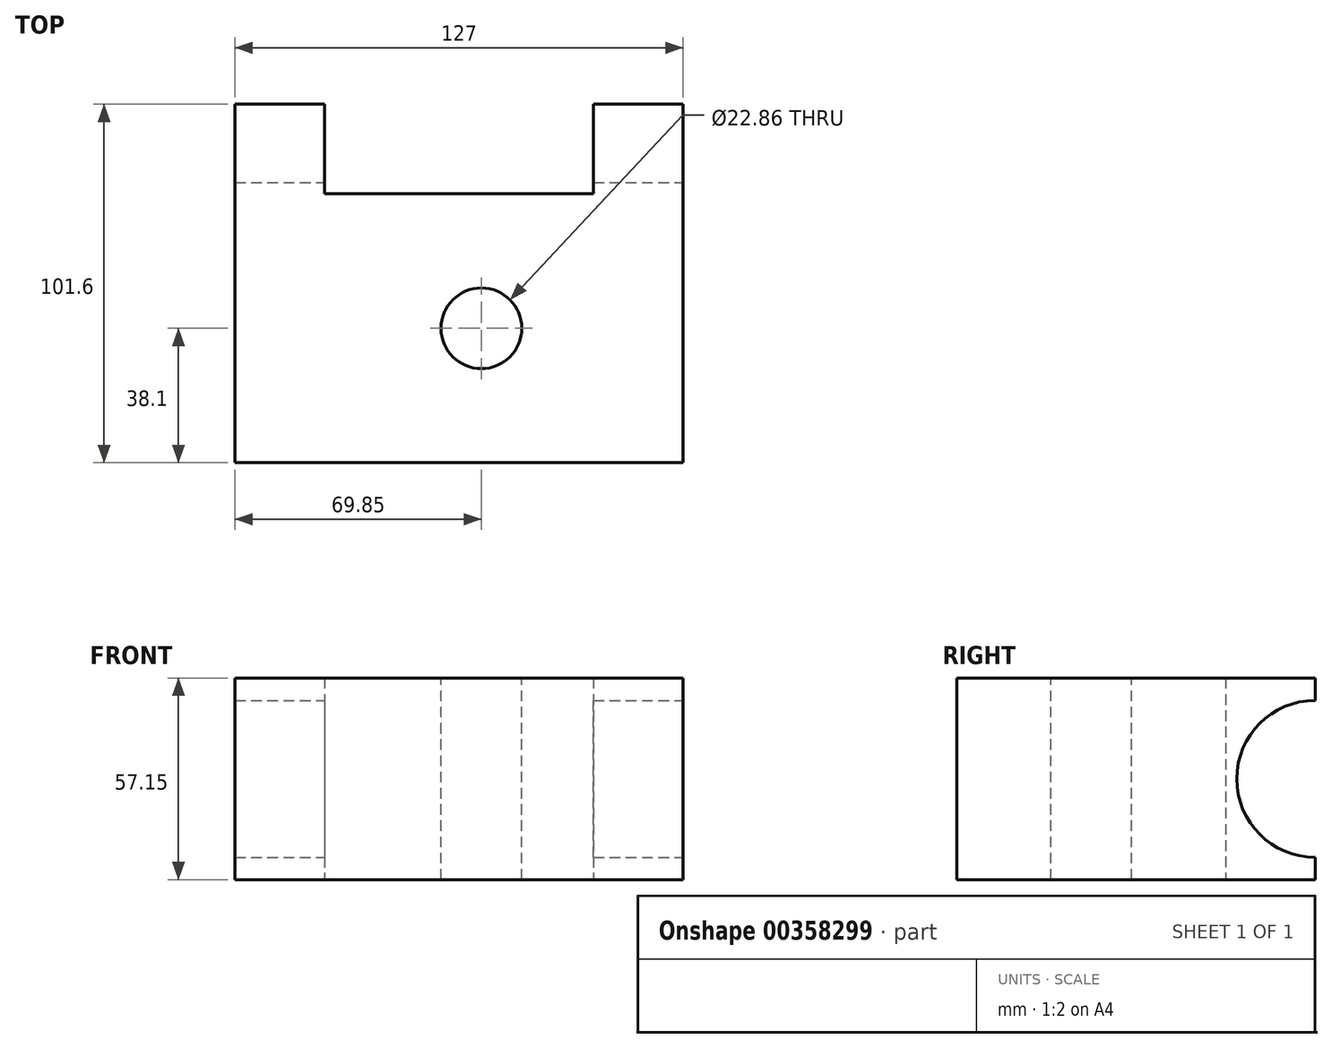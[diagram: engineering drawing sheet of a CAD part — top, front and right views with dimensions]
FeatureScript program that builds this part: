
annotation { "Feature Type Name" : "Feature", "Feature Type Description" : "" }
export const myFeature = defineFeature(function(context is Context, id is Id, definition is map)
    precondition{}
    {
        {
            var Q0;
            Q0=qCreatedBy(makeId("Top.planeOp"),FACE);
            var sketch = newSketch(context, id + "F0", { "sketchPlane" : qUnion([Q0])});
            skLineSegment(sketch, "E0.bottom", {"start": v(0, 0) * mm, "end": v(127, 0) * mm});
            skLineSegment(sketch, "E0.top", {"start": v(0, 101.6) * mm, "end": v(25.4, 101.6) * mm});
            skLineSegment(sketch, "E0.left", {"start": v(0, 0) * mm, "end": v(0, 101.6) * mm});
            skLineSegment(sketch, "E0.right", {"start": v(127, 0) * mm, "end": v(127, 101.6) * mm});
            skLineSegment(sketch, "E1", {"start": v(25.4, 101.6) * mm, "end": v(25.4, 76.2) * mm});
            skLineSegment(sketch, "E2", {"start": v(25.4, 76.2) * mm, "end": v(101.6, 76.2) * mm});
            skLineSegment(sketch, "E3", {"start": v(101.6, 76.2) * mm, "end": v(101.6, 101.6) * mm});
            skLineSegment(sketch, "E4.trimOffspring", {"start": v(101.6, 101.6) * mm, "end": v(127, 101.6) * mm});
            skSolve(sketch);
        }
        {
            var Q0;
            Q0 = qSketchRegion(id + "F0", true);
            extrude(context, id + "F1", {"entities" : qUnion([Q0]), "depth" : 57.15 * mm});
        }
        {
            var Q0;
            Q0=makeQuery(id+"F1.opExtrude","SWEPT_FACE",FACE,{"disambiguationData":[OSD([sQuery(id+"F0.wireOp",EDGE,"E0.right")])]});
            var sketch = newSketch(context, id + "F2", { "sketchPlane" : qUnion([Q0])});
            skCircle(sketch, "E5", {"center": v(101.6, 28.58) * mm, "radius": 22.23 * mm});
            skSolve(sketch);
        }
        {
            var Q0;
            Q0 = qSketchRegion(id + "F2", true);
            extrude(context, id + "F3", {"entities" : qUnion([Q0]), "operationType" : NewBodyOperationType.REMOVE, "oppositeDirection" : true, "depth" : 127 * mm});
        }
        {
            var Q0;
            Q0=makeQuery(id+"F1.opExtrude","CAP_FACE",FACE,{"disambiguationData":[OSD([sQuery(id+"F0.wireOp",EDGE,"E0.bottom"),sQuery(id+"F0.wireOp",EDGE,"E0.top"),sQuery(id+"F0.wireOp",EDGE,"E0.left"),sQuery(id+"F0.wireOp",EDGE,"E0.right"),sQuery(id+"F0.wireOp",EDGE,"E1"),sQuery(id+"F0.wireOp",EDGE,"E2"),sQuery(id+"F0.wireOp",EDGE,"E3"),sQuery(id+"F0.wireOp",EDGE,"E4.trimOffspring")])],"isStart":false});
            var sketch = newSketch(context, id + "F4", { "sketchPlane" : qUnion([Q0])});
            skCircle(sketch, "E6", {"center": v(69.85, 38.1) * mm, "radius": 11.43 * mm});
            skSolve(sketch);
        }
        {
            var Q0;
            Q0 = qSketchRegion(id + "F4", true);
            extrude(context, id + "F5", {"entities" : qUnion([Q0]), "operationType" : NewBodyOperationType.REMOVE, "oppositeDirection" : true, "depth" : 76.2 * mm});
        }
    });
